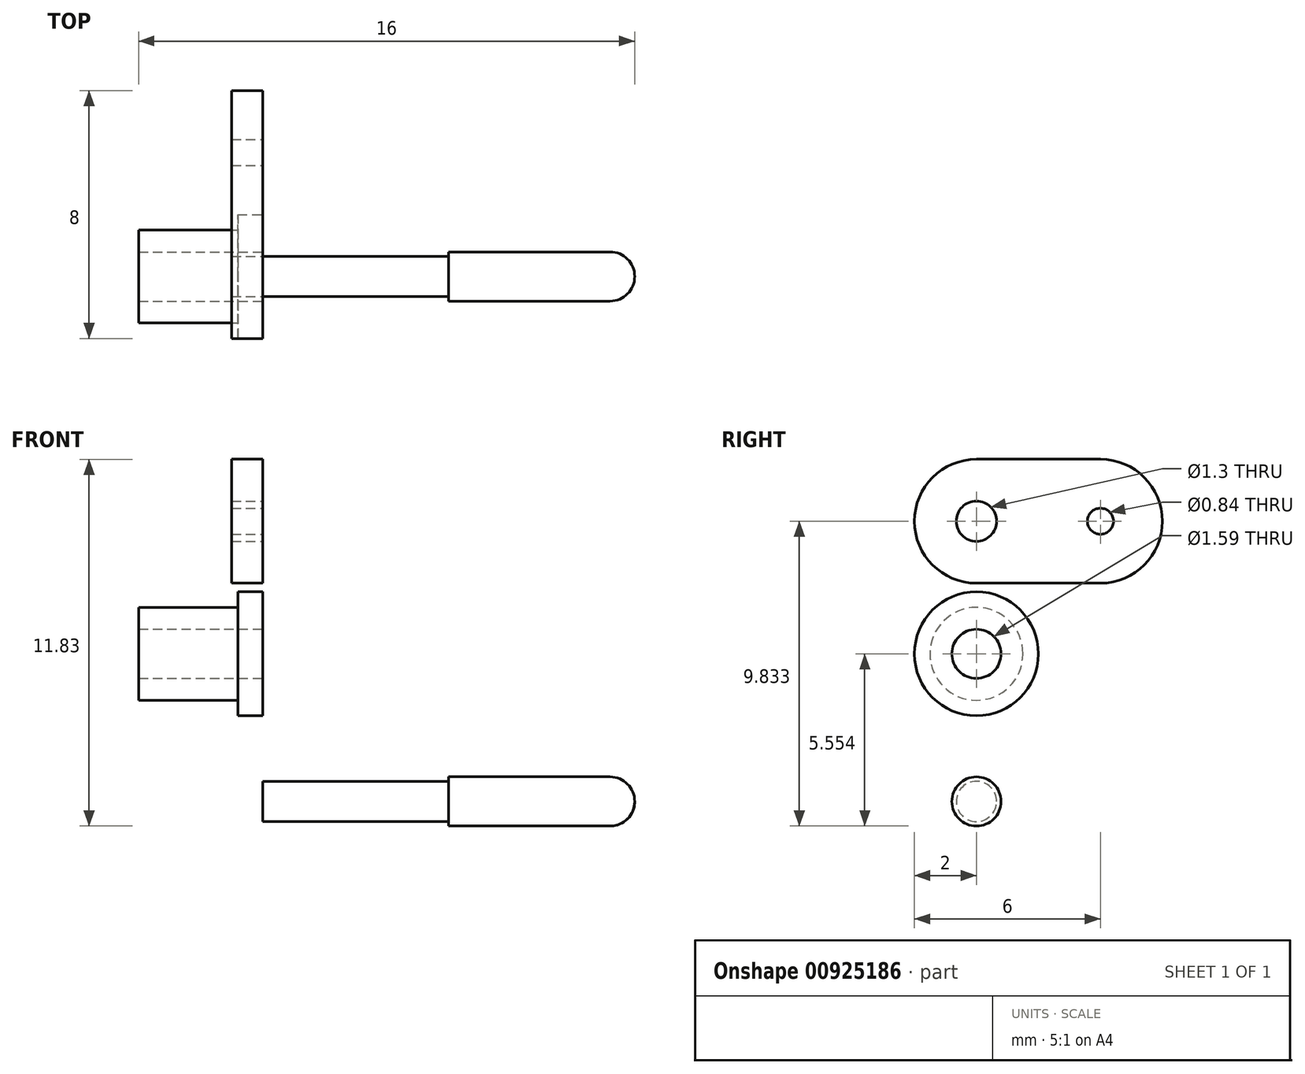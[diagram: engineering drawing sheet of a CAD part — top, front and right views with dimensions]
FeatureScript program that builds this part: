
annotation { "Feature Type Name" : "Feature", "Feature Type Description" : "" }
export const myFeature = defineFeature(function(context is Context, id is Id, definition is map)
    precondition{}
    {
        {
            var Q0;
            Q0=qCreatedBy(makeId("Front.planeOp"),FACE);
            var sketch = newSketch(context, id + "F0", { "sketchPlane" : qUnion([Q0])});
            skLineSegment(sketch, "E0.bottom", {"start": v(0, 0) * mm, "end": v(6, 0) * mm});
            skLineSegment(sketch, "E0.top", {"start": v(0, 0.65) * mm, "end": v(6, 0.65) * mm});
            skLineSegment(sketch, "E0.left", {"start": v(0, 0) * mm, "end": v(0, 0.65) * mm});
            skLineSegment(sketch, "E0.right", {"start": v(6, 0) * mm, "end": v(6, 0.65) * mm});
            skLineSegment(sketch, "E1.bottom", {"start": v(6, 0) * mm, "end": v(12, 0) * mm});
            skLineSegment(sketch, "E1.top", {"start": v(6, 0.8) * mm, "end": v(11.2, 0.8) * mm});
            skLineSegment(sketch, "E1.left", {"start": v(6, 0) * mm, "end": v(6, 0.8) * mm});
            skLineSegment(sketch, "E1.right", {"start": v(12, 0) * mm, "end": v(12, 0) * mm});
            skPoint(sketch, "E2.visualSharp", {"position": v(12, 0.8) * mm});
            skArc(sketch, "E2.filletArc", {"start": v(12, 0) * mm, "mid": v(11.77, 0.56) * mm, "end": v(11.2, 0.8) * mm});
            skSolve(sketch);
        }
        {
            var Q0;
            Q0=makeQuery(id+"F0.imprint","IMPRINT",FACE,{"disambiguationData":[TD([[makeQuery(id+"F0.imprint","IMPRINT",EDGE,{"derivedFrom":sQuery(id+"F0.wireOp",EDGE,"E0.bottom")}),1.0]])]});
            var Q1;
            Q1=makeQuery(id+"F0.imprint","IMPRINT",FACE,{"disambiguationData":[TD([[makeQuery(id+"F0.imprint","IMPRINT",EDGE,{"derivedFrom":sQuery(id+"F0.wireOp",EDGE,"E0.right")}),-1.0]])]});
            var Q2;
            Q2=sQuery(id+"F0.wireOp",EDGE,"E0.bottom");
            revolve(context, id + "F1", {"surfaceOperationType" : NewSurfaceOperationType.NEW, "entities" : qUnion([Q0, Q1]), "axis" : qUnion([Q2]), "revolveType" : RevolveType.FULL});
        }
        {
            var Q0;
            Q0=qCreatedBy(makeId("Front.planeOp"),FACE);
            var sketch = newSketch(context, id + "F2", { "sketchPlane" : qUnion([Q0])});
            skLineSegment(sketch, "E3.bottom", {"start": v(0, 2.76) * mm, "end": v(-0.8, 2.76) * mm});
            skLineSegment(sketch, "E3.top", {"start": v(0, 4.76) * mm, "end": v(-0.8, 4.76) * mm});
            skLineSegment(sketch, "E3.left", {"start": v(0, 2.76) * mm, "end": v(0, 4.76) * mm});
            skLineSegment(sketch, "E3.right", {"start": v(-0.8, 2.76) * mm, "end": v(-0.8, 3.26) * mm});
            skLineSegment(sketch, "E4.bottom", {"start": v(-0.8, 4.76) * mm, "end": v(-4, 4.76) * mm});
            skLineSegment(sketch, "E4.top", {"start": v(-0.8, 3.26) * mm, "end": v(-4, 3.26) * mm});
            skLineSegment(sketch, "E4.right", {"start": v(-4, 4.76) * mm, "end": v(-4, 3.26) * mm});
            skLineSegment(sketch, "E5.bottom", {"start": v(0, 4.76) * mm, "end": v(-4, 4.76) * mm});
            skLineSegment(sketch, "E5.top", {"start": v(0, 3.97) * mm, "end": v(-4, 3.97) * mm});
            skLineSegment(sketch, "E5.left", {"start": v(0, 4.76) * mm, "end": v(0, 3.97) * mm});
            skLineSegment(sketch, "E5.right", {"start": v(-4, 4.76) * mm, "end": v(-4, 3.97) * mm});
            skLineSegment(sketch, "E6", {"start": v(0, 0) * mm, "end": v(0, 4.76) * mm, "construction": true});
            skSolve(sketch);
        }
        {
            var Q0;
            Q0=makeQuery(id+"F2.imprint","IMPRINT",FACE,{"disambiguationData":[TD([[makeQuery(id+"F2.imprint","IMPRINT",EDGE,{"derivedFrom":sQuery(id+"F2.wireOp",EDGE,"E3.bottom")}),-1.0]])]});
            var Q1;
            Q1=sQuery(id+"F2.wireOp",EDGE,"E4.bottom");
            revolve(context, id + "F3", {"surfaceOperationType" : NewSurfaceOperationType.NEW, "entities" : qUnion([Q0]), "axis" : qUnion([Q1]), "revolveType" : RevolveType.FULL});
        }
        {
            var Q0;
            Q0=qCreatedBy(makeId("Right.planeOp"),FACE);
            var sketch = newSketch(context, id + "F4", { "sketchPlane" : qUnion([Q0])});
            skLineSegment(sketch, "E7", {"start": v(0, 9.04) * mm, "end": v(8.78, 9.04) * mm, "construction": true});
            skArc(sketch, "E8", {"start": v(0, 11.04) * mm, "mid": v(-2, 9.04) * mm, "end": v(0, 7.04) * mm});
            skArc(sketch, "E9", {"start": v(4, 7.04) * mm, "mid": v(6, 9.04) * mm, "end": v(4, 11.04) * mm});
            skLineSegment(sketch, "E10", {"start": v(0, 11.04) * mm, "end": v(4, 11.04) * mm});
            skLineSegment(sketch, "E11", {"start": v(0, 7.04) * mm, "end": v(4, 7.04) * mm});
            skCircle(sketch, "E12", {"center": v(0, 9.04) * mm, "radius": 0.65 * mm});
            skCircle(sketch, "E13", {"center": v(4, 9.04) * mm, "radius": 0.42 * mm});
            skSolve(sketch);
        }
        {
            var Q0;
            Q0=makeQuery(id+"F4.imprint","IMPRINT",FACE,{"disambiguationData":[TD([[makeQuery(id+"F4.imprint","IMPRINT",EDGE,{"derivedFrom":sQuery(id+"F4.wireOp",EDGE,"E8")}),1.0]])]});
            extrude(context, id + "F5", {"entities" : qUnion([Q0]), "oppositeDirection" : true, "depth" : 1 * mm, "offsetDistance" : 25 * mm});
        }
    });
